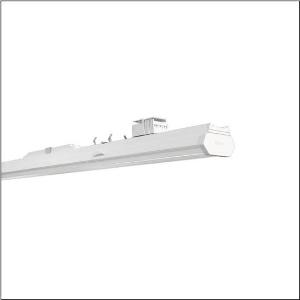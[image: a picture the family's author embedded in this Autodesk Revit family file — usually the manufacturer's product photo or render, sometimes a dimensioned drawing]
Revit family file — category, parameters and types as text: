
# Revit family: licross_r__11_protected_ho_51td12dn4fxm3c_9ee7
name_source: partatom
category: Lighting Fixtures
units: mm (PartAtom-declared; Revit-internal decimal feet)

## family parameters
Cut with Voids When Loaded = No
Host = Face
Light Source = No
Part Type = Normal
Room Calculation Point = No
Round Connector Dimension = Use Diameter
Shared = No

## types (1)
- --- (1 x LED, 970 lm, 7.4 W, 4000K)
    Apparent Load = 7 VA
    CIE Flux Codes = 70 91 97 98 100
    Color Rendering = 80
    Color Temperature = 4000K
    Default Elevation = 1800 mm
    Description = Licross® 11 Protected HO, luminaire insert, of sheet steel, galvanised, coil coated, white, length: 1.500mm, width: 90mm, height: 101mm, LED rated luminous flux: 15.270lm, light colour: 840, control gear: DALI 2, with plug, 6-pole, with phase selection, for trunking rail, 14-core, mains connection: 220..240V, AC, 50/60Hz, rated input power: 91W, for trunking rail, 14-core, halogen-free wiring, for emergency light function, converter,control gear: single battery element, battery: LiFeP04, 9Ah, primary light control with lens, of plastic, primary optical cover: cover, of PMMA, light emission: direct distribution, primary light characteristic: symmetric, protection rating (complete): IP54, insulation class (complete): insulation class I (protective earthing), certification: CE, UKCA, protection symbol: D if used in an environment with non-conductive dust loads with corresponding accessories, impact resistance: IK06, permissible ambient temperature for indoor applications: +5..+30°C, standard: EN 60598-2-22, LABS conformity tested according to VDMA 24364:2018-05, reducing of maximum allowable ambient temperature of 5°C with ceiling mounting, corresponds to IFS (International Featured Standards) requirements for safety and quality in the food industry, packaging unit: 1 piece
    Height = 92 mm
    Lamp = 1 x LED
    Lamp Light Flux = 970 lm
    Lamp Power = 7.4 W
    Lamp count = 1
    Length = 1500 mm
    Luminous efficacy = 131 lm/W
    Manufacturer = Siteco
    ModVariant = No
    Model = 51TD12DN4FXM3C
    Mounting Place = Ceiling
    Mounting Type = Pendant
    Number of Poles = 1
    OnlyDefault = Yes
    Power Factor = 1
    Product Name = Licross® 11 Protected HO
    Product group = luminaire insert
    ProductGroupID = 901
    Protection Class = Protection class I
    Protection Degree = IP 54
    RLX_Detail_Level = 1
    RLX_Emergency_Light_Flux = 0 lm
    RLX_Emergency_Type = 0
    RLX_Emergency_Type_DB = No
    RlxData = <blob elided: 24801 chars, md5=f153839c>
    Socket = socket
    Standby Power = 0 W
    System Light Flux = 970 lm
    System Power = 7 W
    Type Comments = : emergency light operation: 3 h
    Type Image = l_1256145.jpg
    URL = http://relux.com
    VarID = @adj_041481
    Voltage = 0 V
    Weight = 0.00 kg
    Width = 88 mm

## geometry (parser evidence)
native form markers: Blend x4, Sweep x10
no freeform markers — native parametric forms only
